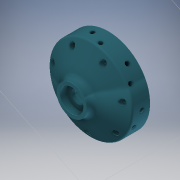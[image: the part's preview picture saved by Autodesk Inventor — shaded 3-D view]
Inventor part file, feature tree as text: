
AUTODESK INVENTOR PART (.ipt)
format: ipt  version: 2018 (Build 220112000, 112)  size: 406,016 bytes
history: native  units: mm
features: sketch x5, revolve x2, extrude x2, hole x1, other x1, pattern_circular x1, projected_geometry x1
ambient origin geometry x8: Origin, YZ Plane, XZ Plane, XY Plane, X Axis, Y Axis, Z Axis, Center Point
bodies: Solid1 (feature_tree)
feature tree (13):
  revolve  "Revolution1"  [1 undecoded]
  extrude  "Extrusion1"  Depth=6.0mm
  hole  "Hole1"  [1 undecoded]
  revolve  "Revolution2"  [1 undecoded]
  extrude  "Extrusion2"  Depth=10.0mm
  other  "Work Axis1"
  pattern_circular  "Circular Pattern1"  [2 undecoded]
  sketch  "Sketch1"  dims[d0=50.0mm d1=45.0mm]
  sketch  "Sketch2"  dims[d2=40.5mm d3=6.0mm]
  sketch  "Sketch3"  dims[d4=32.5mm d5=44.0mm]
  sketch  "Sketch4"  dims[d6=3.5mm d7=18.0mm]
  sketch  "Sketch5"  dims[d8=14.0mm d9=4.63734mm d10=8.0mm d11=3.5mm d12=8.0mm d13=3.0mm d14=90.0deg d15=5.0mm d16=7.0mm d17=9.0mm d18=10.0mm d19=16.5mm d20=59.5mm d21=0.0mm d23=4.0mm d24=6.0mm d25=4.0mm d26=2.0mm d27=90.0deg d28=24.5mm d29=0.0mm d30=3.5mm d32=5.0mm d33=90.0deg d34=70.0mm d35=360.0deg d37=21.0mm d38=42.5mm d39=5.0mm d40=10.0mm d41=0.0mm d42=22.5mm]
  projected_geometry  "Projected Loop1"
note: 5 required parameter values undecoded (feature->parameter linkage not recoverable at this tier; creation-order binding heuristic only, values carry confidence <= 0.55)